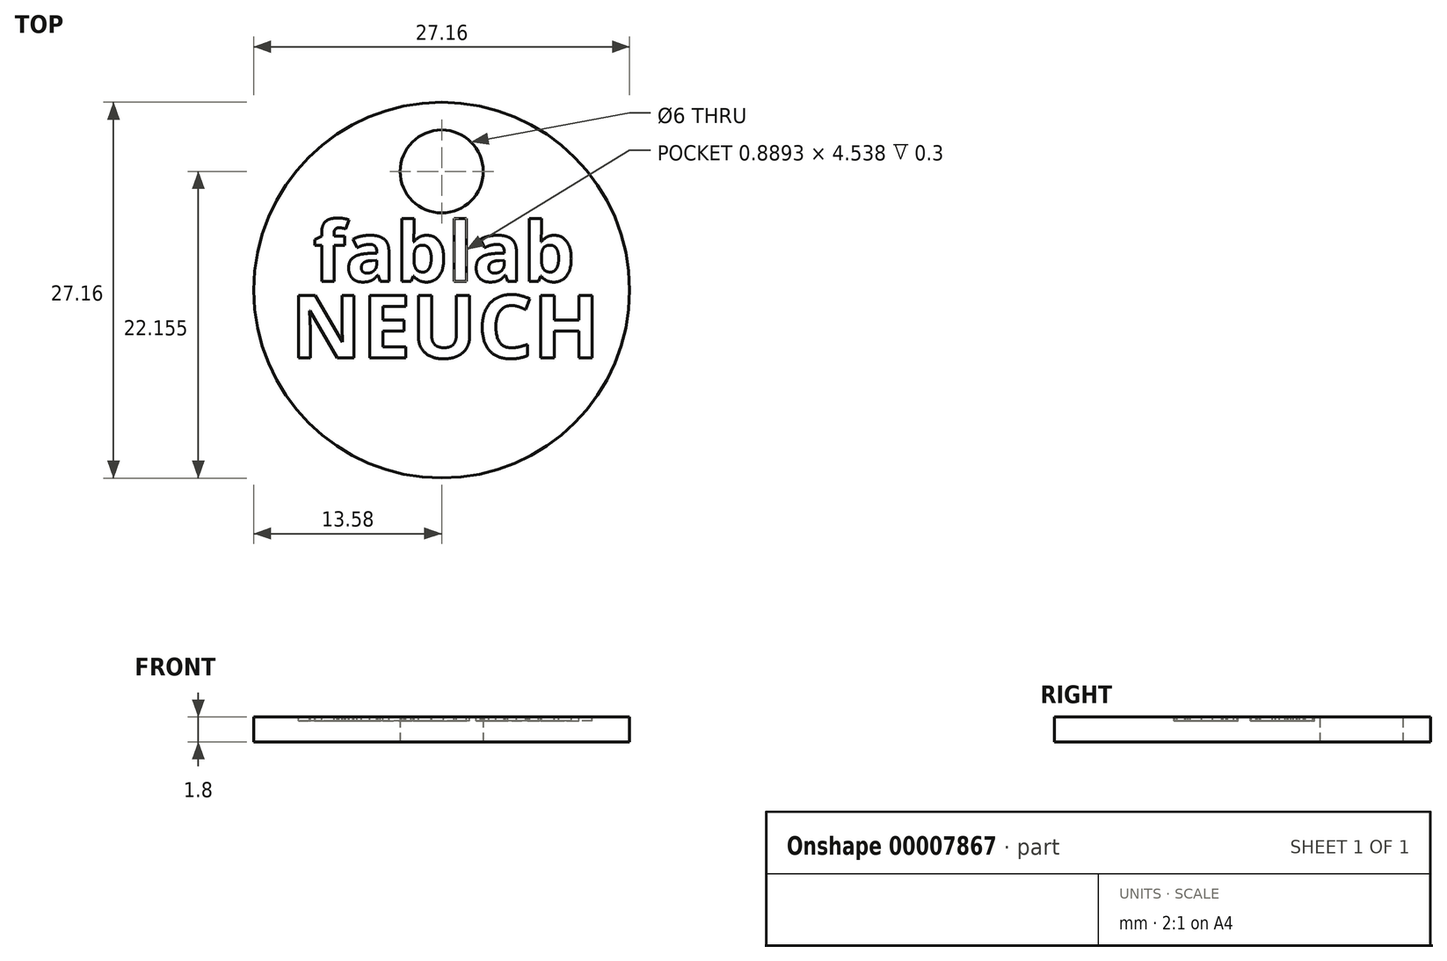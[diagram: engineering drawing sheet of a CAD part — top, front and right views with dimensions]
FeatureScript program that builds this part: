
annotation { "Feature Type Name" : "Feature", "Feature Type Description" : "" }
export const myFeature = defineFeature(function(context is Context, id is Id, definition is map)
    precondition{}
    {
        {
            var Q0;
            Q0=qCreatedBy(makeId("Top.planeOp"),FACE);
            var sketch = newSketch(context, id + "F0", { "sketchPlane" : qUnion([Q0])});
            skCircle(sketch, "E0", {"center": v(0, 0) * mm, "radius": 13.58 * mm});
            skCircle(sketch, "E1", {"center": v(0, 8.57) * mm, "radius": 3 * mm});
            skSolve(sketch);
        }
        {
            var Q0;
            Q0=makeQuery(id+"F0.imprint","IMPRINT",FACE,{"disambiguationData":[TD([[makeQuery(id+"F0.imprint","IMPRINT",EDGE,{"derivedFrom":sQuery(id+"F0.wireOp",EDGE,"E0")}),1.0]])]});
            extrude(context, id + "F1", {"entities" : qUnion([Q0]), "depth" : 1.8 * mm});
        }
        {
            var Q0;
            Q0=makeQuery(id+"F1.opExtrude","CAP_FACE",FACE,{"disambiguationData":[OSD([sQuery(id+"F0.wireOp",EDGE,"E0"),sQuery(id+"F0.wireOp",EDGE,"E1")])],"isStart":false});
            var sketch = newSketch(context, id + "F2", { "sketchPlane" : qUnion([Q0])});
            skSolve(sketch);
        }
        {
            var Q0;
            Q0=makeQuery(id+"F2.imprint","IMPRINT",FACE,{"disambiguationData":[TD([[makeQuery(id+"F2.imprint","IMPRINT",EDGE,{"derivedFrom":makeQuery(id+"F1.opExtrude","CAP_EDGE",EDGE,{"disambiguationData":[OSD([sQuery(id+"F0.wireOp",EDGE,"E0")])],"isStart":false})}),1.0]])]});
            var sketch = newSketch(context, id + "F3", { "sketchPlane" : qUnion([Q0])});
            skText(sketch, "E2", { "text": "fablab", "fontName": "OpenSans-Bold.ttf"});
            const initialGuessF3  = {"E2": [-0.00928, 0.00064, 1, 0, 0.0043]};
            skSetInitialGuess(sketch, initialGuessF3);
            skSolve(sketch);
        }
        {
            var Q0;
            Q0 = qSketchRegion(id + "F3", true);
            extrude(context, id + "F4", {"entities" : qUnion([Q0]), "operationType" : NewBodyOperationType.REMOVE, "oppositeDirection" : true, "depth" : 0.3 * mm});
        }
        {
            var Q0;
            Q0=makeQuery(id+"F3.imprint","IMPRINT",FACE,{"disambiguationData":[TD([[makeQuery(id+"F3.imprint","IMPRINT",EDGE,{"derivedFrom":sQuery(id+"F3.wireOp",EDGE,"E2.sketch_text.stroke-0")}),1.0]])]});
            var sketch = newSketch(context, id + "F5", { "sketchPlane" : qUnion([Q0])});
            skText(sketch, "E3", { "text": "NEUCH", "fontName": "OpenSans-Bold.ttf"});
            const initialGuessF5  = {"E3": [-0.01092, -0.0049, 1, 0, 0.00456]};
            skSetInitialGuess(sketch, initialGuessF5);
            skSolve(sketch);
        }
        {
            var Q0;
            Q0 = qSketchRegion(id + "F5", true);
            extrude(context, id + "F6", {"entities" : qUnion([Q0]), "operationType" : NewBodyOperationType.REMOVE, "oppositeDirection" : true, "depth" : 0.3 * mm});
        }
    });
